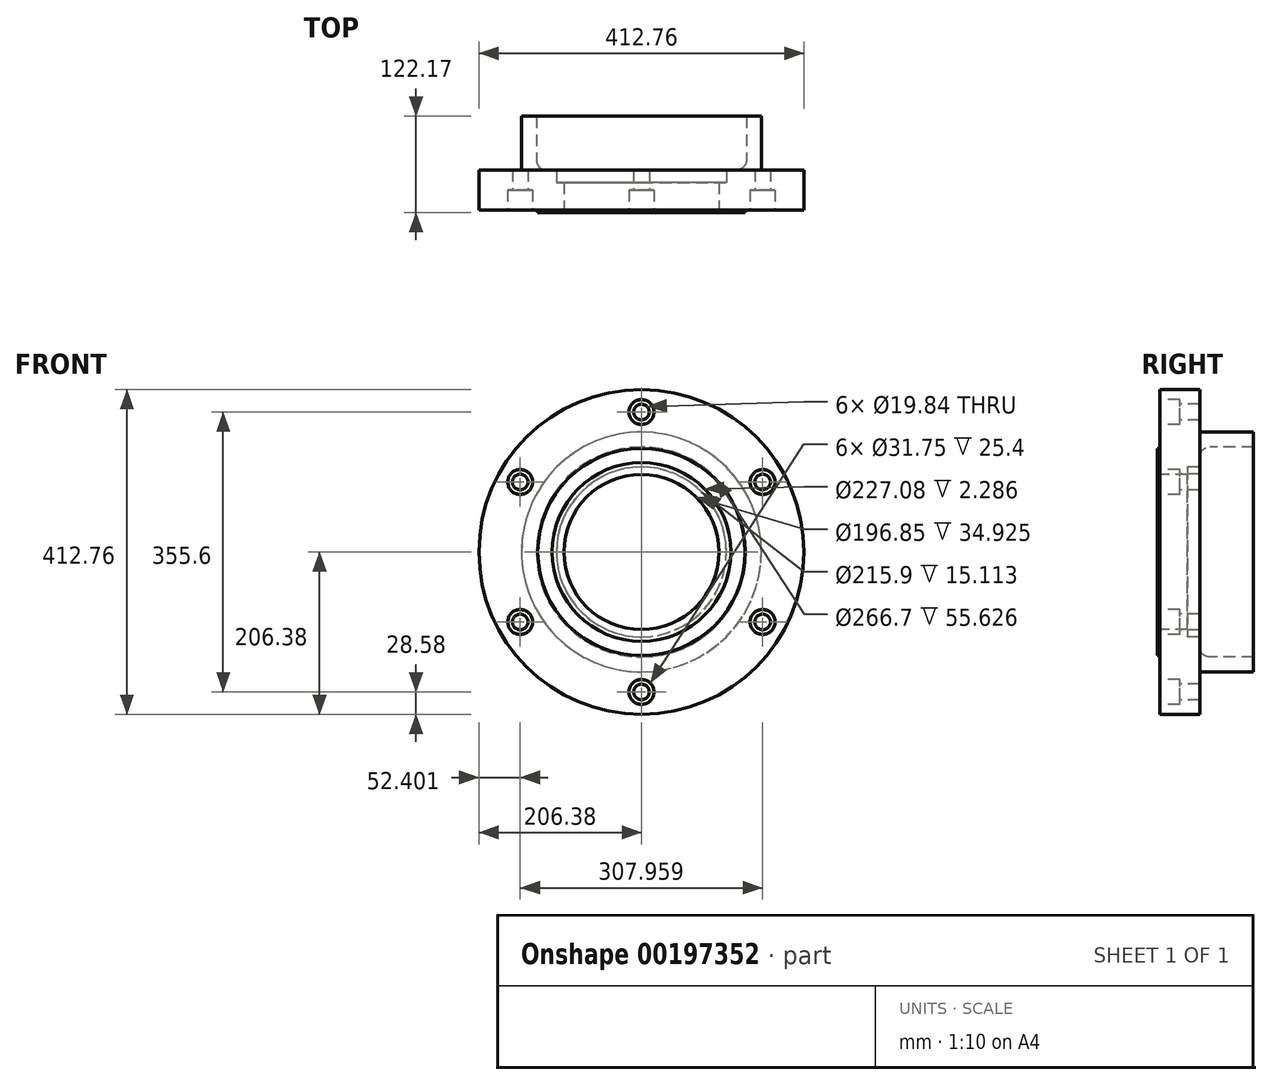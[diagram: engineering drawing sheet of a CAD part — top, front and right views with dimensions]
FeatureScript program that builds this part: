
annotation { "Feature Type Name" : "Feature", "Feature Type Description" : "" }
export const myFeature = defineFeature(function(context is Context, id is Id, definition is map)
    precondition{}
    {
        {
            var Q0;
            Q0=qCreatedBy(makeId("Right.planeOp"),FACE);
            var sketch = newSketch(context, id + "F0", { "sketchPlane" : qUnion([Q0])});
            skLineSegment(sketch, "E0", {"start": v(-145.85, 0) * mm, "end": v(147.56, 0) * mm, "construction": true});
            skLineSegment(sketch, "E1", {"start": v(0, 131.71) * mm, "end": v(0, 113.54) * mm});
            skLineSegment(sketch, "E2.0", {"start": v(-145.85, 98.43) * mm, "end": v(147.56, 98.43) * mm, "construction": true});
            skLineSegment(sketch, "E3.0", {"start": v(-124.97, 206.38) * mm, "end": v(168.45, 206.38) * mm, "construction": true});
            skPoint(sketch, "E4.orphan", {"position": v(0, 121.54) * mm});
            skLineSegment(sketch, "E5.0", {"start": v(3.05, 206.38) * mm, "end": v(3.05, 131.71) * mm});
            skLineSegment(sketch, "E6.trimOffspring", {"start": v(3.05, 0) * mm, "end": v(3.05, -96.9) * mm, "construction": true});
            skLineSegment(sketch, "E7.0", {"start": v(0, 131.71) * mm, "end": v(3.05, 131.71) * mm});
            skLineSegment(sketch, "E8.0", {"start": v(0, 113.54) * mm, "end": v(3.05, 113.54) * mm});
            skLineSegment(sketch, "E9.trimOffspring", {"start": v(0, 0) * mm, "end": v(0, -96.9) * mm, "construction": true});
            skLineSegment(sketch, "E10.trimOffspring", {"start": v(3.05, 113.54) * mm, "end": v(3.05, 98.43) * mm});
            skLineSegment(sketch, "E11", {"start": v(3.05, 206.38) * mm, "end": v(53.85, 206.38) * mm});
            skLineSegment(sketch, "E12.0", {"start": v(53.85, 152.4) * mm, "end": v(122.17, 152.4) * mm});
            skLineSegment(sketch, "E13", {"start": v(53.85, 206.38) * mm, "end": v(53.85, 152.4) * mm});
            skLineSegment(sketch, "E14.0", {"start": v(122.17, 152.4) * mm, "end": v(122.17, 133.35) * mm});
            skLineSegment(sketch, "E15.0", {"start": v(53.85, 133.35) * mm, "end": v(122.17, 133.35) * mm});
            skLineSegment(sketch, "E16", {"start": v(53.85, 133.35) * mm, "end": v(53.85, 107.95) * mm});
            skLineSegment(sketch, "E17.0", {"start": v(37.97, 107.95) * mm, "end": v(53.85, 107.95) * mm});
            skLineSegment(sketch, "E18.0", {"start": v(37.97, 107.95) * mm, "end": v(37.97, 98.43) * mm});
            skLineSegment(sketch, "E19", {"start": v(3.05, 98.43) * mm, "end": v(37.97, 98.43) * mm});
            skSolve(sketch);
        }
        {
            var Q0;
            Q0=makeQuery(id+"F0.imprint","IMPRINT",FACE,{"disambiguationData":[TD([[makeQuery(id+"F0.imprint","IMPRINT",EDGE,{"derivedFrom":sQuery(id+"F0.wireOp",EDGE,"E1")}),1.0]])]});
            var Q1;
            Q1=sQuery(id+"F0.wireOp",EDGE,"E0");
            revolve(context, id + "F1", {"entities" : qUnion([Q0]), "axis" : qUnion([Q1]), "revolveType" : RevolveType.FULL});
        }
        {
            var Q0;
            Q0=makeQuery(id+"F1.opRevolve","SWEPT_EDGE",EDGE,{"disambiguationData":[OSD([sQuery(id+"F0.wireOp",EDGE,"E15.0"),sQuery(id+"F0.wireOp",EDGE,"E16")])]});
            fillet(context, id + "F2", {"entities" : qUnion([Q0]), "radius" : 12.7 * mm, "tangentPropagation" : true, "allowEdgeOverflow" : false});
        }
        {
            var Q0;
            Q0=makeQuery(id+"F1.opRevolve","SWEPT_EDGE",EDGE,{"disambiguationData":[OSD([sQuery(id+"F0.wireOp",EDGE,"E12.0"),sQuery(id+"F0.wireOp",EDGE,"E13")])]});
            fillet(context, id + "F3", {"entities" : qUnion([Q0]), "radius" : 2.3 * mm, "tangentPropagation" : true, "allowEdgeOverflow" : false});
        }
        {
            var Q0;
            Q0=makeQuery(id+"F1.opRevolve","SWEPT_EDGE",EDGE,{"disambiguationData":[OSD([sQuery(id+"F0.wireOp",EDGE,"E17.0"),sQuery(id+"F0.wireOp",EDGE,"E18.0")])]});
            fillet(context, id + "F4", {"entities" : qUnion([Q0]), "radius" : 0.76 * mm, "tangentPropagation" : true, "allowEdgeOverflow" : false});
        }
        {
            var Q0;
            Q0=makeQuery(id+"F1.opRevolve","SWEPT_EDGE",EDGE,{"disambiguationData":[OSD([sQuery(id+"F0.wireOp",EDGE,"E5.0"),sQuery(id+"F0.wireOp",EDGE,"E7.0")])]});
            var Q1;
            Q1=makeQuery(id+"F1.opRevolve","SWEPT_EDGE",EDGE,{"disambiguationData":[OSD([sQuery(id+"F0.wireOp",EDGE,"E8.0"),sQuery(id+"F0.wireOp",EDGE,"E10.trimOffspring")])]});
            fillet(context, id + "F5", {"entities" : qUnion([Q0, Q1]), "radius" : 0.76 * mm, "tangentPropagation" : true, "allowEdgeOverflow" : false});
        }
        {
            var Q0;
            Q0=makeQuery(id+"F1.opRevolve","SWEPT_FACE",FACE,{"disambiguationData":[OSD([sQuery(id+"F0.wireOp",EDGE,"E5.0")])]});
            var sketch = newSketch(context, id + "F6", { "sketchPlane" : qUnion([Q0])});
            skCircle(sketch, "E20", {"center": v(0, 0) * mm, "radius": 177.8 * mm, "construction": true});
            skLineSegment(sketch, "E21", {"start": v(0, 0) * mm, "end": v(0, 235.96) * mm, "construction": true});
            skPoint(sketch, "E22", {"position": v(0, 177.8) * mm});
            skPoint(sketch, "E23.1.0", {"position": v(-153.98, 88.9) * mm});
            skPoint(sketch, "E23.2.0", {"position": v(-153.98, -88.9) * mm});
            skPoint(sketch, "E23.3.0", {"position": v(0, -177.8) * mm});
            skPoint(sketch, "E23.4.0", {"position": v(153.98, -88.9) * mm});
            skPoint(sketch, "E23.5.0", {"position": v(153.98, 88.9) * mm});
            skSolve(sketch);
        }
        {
            var Q0;
            Q0=sQuery(id+"F6.wireOp",VERTEX,"E22");
            var Q1;
            Q1=sQuery(id+"F6.wireOp",VERTEX,"E23.5.0");
            var Q2;
            Q2=sQuery(id+"F6.wireOp",VERTEX,"E23.4.0");
            var Q3;
            Q3=sQuery(id+"F6.wireOp",VERTEX,"E23.3.0");
            var Q4;
            Q4=sQuery(id+"F6.wireOp",VERTEX,"E23.2.0");
            var Q5;
            Q5=sQuery(id+"F6.wireOp",VERTEX,"E23.1.0");
            var Q6;
            Q6=makeQuery(id+"F1.opRevolve","SWEPT_BODY",BODY,{"disambiguationData":[OSD([sQuery(id+"F0.wireOp",EDGE,"E1"),sQuery(id+"F0.wireOp",EDGE,"E5.0"),sQuery(id+"F0.wireOp",EDGE,"E7.0"),sQuery(id+"F0.wireOp",EDGE,"E8.0"),sQuery(id+"F0.wireOp",EDGE,"E10.trimOffspring"),sQuery(id+"F0.wireOp",EDGE,"E11"),sQuery(id+"F0.wireOp",EDGE,"E12.0"),sQuery(id+"F0.wireOp",EDGE,"E13"),sQuery(id+"F0.wireOp",EDGE,"E14.0"),sQuery(id+"F0.wireOp",EDGE,"E15.0"),sQuery(id+"F0.wireOp",EDGE,"E16"),sQuery(id+"F0.wireOp",EDGE,"E17.0"),sQuery(id+"F0.wireOp",EDGE,"E18.0"),sQuery(id+"F0.wireOp",EDGE,"E19")])]});
            hole(context, id + "F7", {"style" : HoleStyle.C_BORE, "endStyle" : HoleEndStyle.THROUGH, "holeDiameter" : 19.84 * mm, "cBoreDiameter" : 31.75 * mm, "cBoreDepth" : 25.4 * mm, "locations" : qUnion([Q0, Q1, Q2, Q3, Q4, Q5]), "scope" : qUnion([Q6]), "isTappedThrough" : true});
        }
    });
